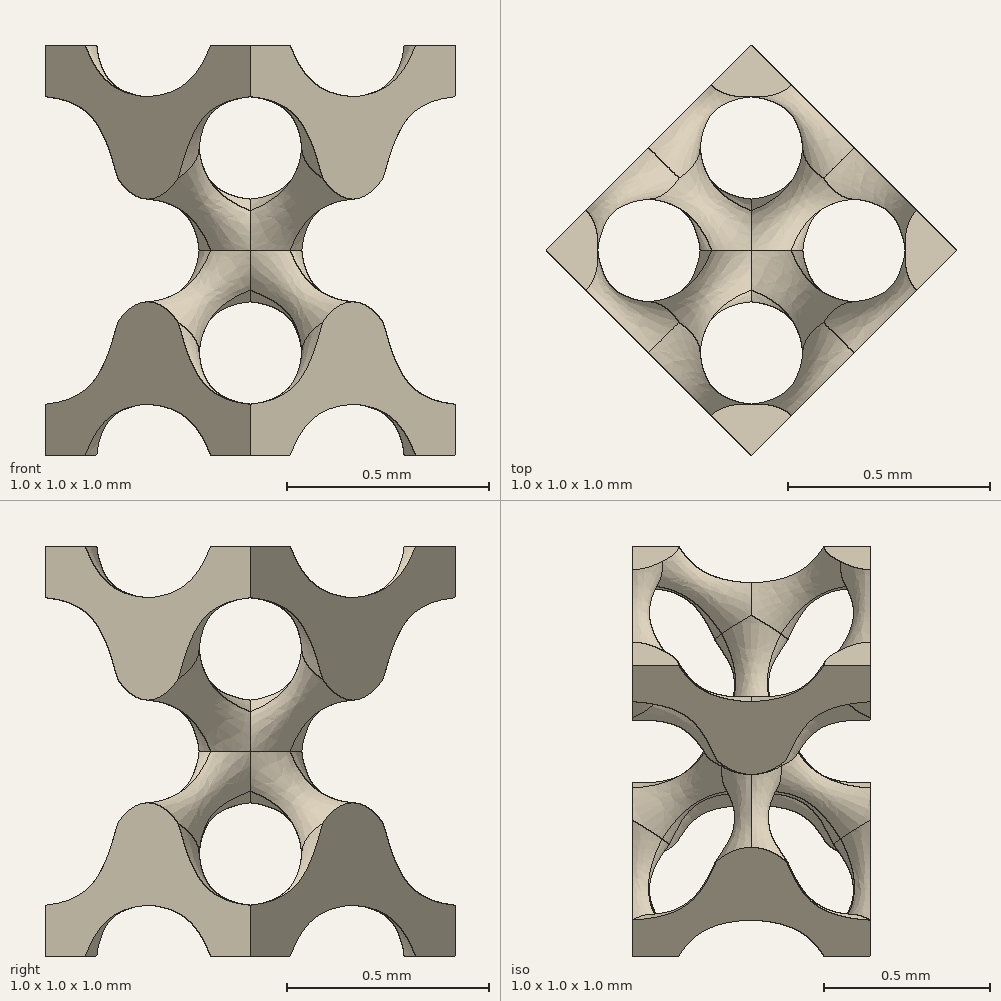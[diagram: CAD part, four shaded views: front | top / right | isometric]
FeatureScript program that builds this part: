
annotation { "Feature Type Name" : "Feature", "Feature Type Description" : "" }
export const myFeature = defineFeature(function(context is Context, id is Id, definition is map)
    precondition{}
    {
        {
            var Q0;
            Q0=qCreatedBy(makeId("Top.planeOp"),FACE);
            var sketch = newSketch(context, id + "F0", { "sketchPlane" : qUnion([Q0])});
            skPoint(sketch, "E0", {"position": v(0.5, 0) * mm});
            skPoint(sketch, "E1", {"position": v(0, -0.5) * mm});
            skLineSegment(sketch, "E2", {"start": v(0, 0) * mm, "end": v(0.5, 0) * mm, "construction": true});
            skLineSegment(sketch, "E3", {"start": v(0, 0) * mm, "end": v(0, -0.5) * mm, "construction": true});
            skSolve(sketch);
        }
        {
            var Q0;
            Q0=qCreatedBy(makeId("Front.planeOp"),FACE);
            cPlane(context, id + "F1", {"entities" : qUnion([Q0]), "cplaneType" : CPlaneType.OFFSET, "offset" : 0.25 * mm, "width" : 152.4 * mm, "height" : 152.4 * mm});
        }
        {
            var Q0;
            Q0=qCreatedBy(id+"F1.planeOp",FACE);
            var sketch = newSketch(context, id + "F2", { "sketchPlane" : qUnion([Q0])});
            skPoint(sketch, "E4", {"position": v(0.25, 0.25) * mm});
            skSolve(sketch);
        }
        {
            var Q0;
            Q0=qCreatedBy(makeId("Front.planeOp"),FACE);
            var sketch = newSketch(context, id + "F3", { "sketchPlane" : qUnion([Q0])});
            skPoint(sketch, "E5", {"position": v(0, 0.5) * mm});
            skSolve(sketch);
        }
        {
            var Q0;
            Q0=sQuery(id+"F3.wireOp",VERTEX,"E5");
            var Q1;
            Q1=qCreatedBy(makeId("Origin.pointOp"),VERTEX);
            var Q2;
            Q2=sQuery(id+"F2.wireOp",VERTEX,"E4");
            cPlane(context, id + "F4", {"entities" : qUnion([Q0, Q1, Q2]), "cplaneType" : CPlaneType.THREE_POINT, "offset" : 25.4 * mm, "width" : 152.4 * mm, "height" : 152.4 * mm});
        }
        {
            var Q0;
            Q0=qCreatedBy(id+"F4.planeOp",FACE);
            var sketch = newSketch(context, id + "F5", { "sketchPlane" : qUnion([Q0])});
            skLineSegment(sketch, "E6", {"start": v(0, 0.5) * mm, "end": v(-0.36, 0.25) * mm, "construction": true});
            skPoint(sketch, "E7", {"position": v(-0.18, 0.38) * mm});
            skLineSegment(sketch, "E8", {"start": v(0, 0.5) * mm, "end": v(-0.18, 0.38) * mm});
            skLineSegment(sketch, "E9", {"start": v(-0.18, 0.38) * mm, "end": v(-0.36, 0.25) * mm});
            skSolve(sketch);
        }
        {
            var Q0;
            Q0=sQuery(id+"F5.wireOp",VERTEX,"E6.start");
            var Q1;
            Q1=sQuery(id+"F5.wireOp",EDGE,"E6");
            cPlane(context, id + "F6", {"entities" : qUnion([Q0, Q1]), "cplaneType" : CPlaneType.LINE_POINT, "offset" : 25.4 * mm, "width" : 152.4 * mm, "height" : 152.4 * mm});
        }
        {
            var Q0;
            Q0=qCreatedBy(id+"F6.planeOp",FACE);
            var sketch = newSketch(context, id + "F7", { "sketchPlane" : qUnion([Q0])});
            skLineSegment(sketch, "E10", {"start": v(0.2, 0.36) * mm, "end": v(0.05, 0.36) * mm});
            skLineSegment(sketch, "E11", {"start": v(0.28, 0.23) * mm, "end": v(0.2, 0.36) * mm});
            skLineSegment(sketch, "E12", {"start": v(0.2, 0.36) * mm, "end": v(0.41, 0) * mm, "construction": true});
            skArc(sketch, "E13", {"start": v(0.28, 0.23) * mm, "mid": v(0.13, 0.23) * mm, "end": v(0.05, 0.36) * mm});
            skLineSegment(sketch, "E14", {"start": v(0.2, 0.36) * mm, "end": v(-0.2, 0.36) * mm, "construction": true});
            skSolve(sketch);
        }
        {
            var Q0;
            Q0=sQuery(id+"F5.wireOp",VERTEX,"E7");
            var Q1;
            Q1=sQuery(id+"F5.wireOp",EDGE,"E6");
            cPlane(context, id + "F8", {"entities" : qUnion([Q0, Q1]), "cplaneType" : CPlaneType.LINE_POINT, "offset" : 25.4 * mm, "width" : 152.4 * mm, "height" : 152.4 * mm});
        }
        {
            var Q0;
            Q0=qCreatedBy(id+"F8.planeOp",FACE);
            var sketch = newSketch(context, id + "F9", { "sketchPlane" : qUnion([Q0])});
            skLineSegment(sketch, "E15", {"start": v(0.16, 0.36) * mm, "end": v(0.2, 0.36) * mm});
            skLineSegment(sketch, "E16.MirrorCS", {"start": v(0.23, 0.32) * mm, "end": v(0.2, 0.36) * mm});
            skLineSegment(sketch, "E17", {"start": v(0.2, 0.36) * mm, "end": v(0.41, 0) * mm, "construction": true});
            skLineSegment(sketch, "E18", {"start": v(0.2, 0.36) * mm, "end": v(-0.2, 0.36) * mm, "construction": true});
            skArc(sketch, "E19", {"start": v(0.23, 0.32) * mm, "mid": v(0.18, 0.32) * mm, "end": v(0.16, 0.36) * mm});
            skSolve(sketch);
        }
        {
            var Q0;
            Q0=sQuery(id+"F2.wireOp",VERTEX,"E4");
            var Q1;
            Q1=sQuery(id+"F5.wireOp",EDGE,"E6");
            cPlane(context, id + "F10", {"entities" : qUnion([Q0, Q1]), "cplaneType" : CPlaneType.LINE_POINT, "offset" : 25.4 * mm, "width" : 152.4 * mm, "height" : 152.4 * mm});
        }
        {
            var Q0;
            Q0=qCreatedBy(id+"F10.planeOp",FACE);
            var sketch = newSketch(context, id + "F11", { "sketchPlane" : qUnion([Q0])});
            skLineSegment(sketch, "E20", {"start": v(0.05, 0.36) * mm, "end": v(0.2, 0.36) * mm});
            skLineSegment(sketch, "E21.MirrorCS", {"start": v(0.28, 0.23) * mm, "end": v(0.2, 0.36) * mm});
            skLineSegment(sketch, "E22", {"start": v(0.41, 0) * mm, "end": v(0.2, 0.36) * mm, "construction": true});
            skLineSegment(sketch, "E23", {"start": v(-0.2, 0.36) * mm, "end": v(0.2, 0.36) * mm, "construction": true});
            skArc(sketch, "E24", {"start": v(0.28, 0.23) * mm, "mid": v(0.13, 0.23) * mm, "end": v(0.05, 0.36) * mm});
            skSolve(sketch);
        }
        {
            var Q0;
            Q0=qSketchRegion(id+"F7",true);
            var Q1;
            Q1=qSketchRegion(id+"F9",true);
            var Q2;
            Q2=qSketchRegion(id+"F11",true);
            loft(context, id + "F12", {"sheetProfilesArray" : [{ "sheetProfileEntities" : qUnion([Q0]) }, { "sheetProfileEntities" : qUnion([Q1]) }, { "sheetProfileEntities" : qUnion([Q2]) }]});
        }
        {
            var Q0;
            Q0=sQuery(id+"F0.wireOp",VERTEX,"E1");
            var Q1;
            Q1=sQuery(id+"F0.wireOp",VERTEX,"E0");
            var Q2;
            Q2=sQuery(id+"F5.wireOp",VERTEX,"E8.start");
            cPlane(context, id + "F13", {"entities" : qUnion([Q0, Q1, Q2]), "cplaneType" : CPlaneType.THREE_POINT, "offset" : 25.4 * mm, "width" : 152.4 * mm, "height" : 152.4 * mm});
        }
        {
            var Q0;
            Q0=qCreatedBy(id+"F13.planeOp",FACE);
            var sketch = newSketch(context, id + "F14", { "sketchPlane" : qUnion([Q0])});
            skLineSegment(sketch, "E25", {"start": v(0, 0) * mm, "end": v(-0.41, 0) * mm, "construction": true});
            skLineSegment(sketch, "E26", {"start": v(0.2, -0.36) * mm, "end": v(-0.41, 0) * mm});
            skLineSegment(sketch, "E27", {"start": v(-0.41, 0) * mm, "end": v(-0.2, 0.36) * mm});
            skLineSegment(sketch, "E28", {"start": v(-0.2, 0.36) * mm, "end": v(0, 0) * mm});
            skLineSegment(sketch, "E29", {"start": v(0.2, -0.36) * mm, "end": v(0.41, 0) * mm});
            skLineSegment(sketch, "E30", {"start": v(0.41, 0) * mm, "end": v(0, 0) * mm});
            skSolve(sketch);
        }
        {
            var Q0;
            Q0=qSketchRegion(id+"F14",true);
            extrude(context, id + "F15", {"entities" : qUnion([Q0]), "operationType" : NewBodyOperationType.REMOVE, "endBound" : BoundingType.THROUGH_ALL, "oppositeDirection" : true, "depth" : 25.4 * mm, "hasSecondDirection" : true, "secondDirectionBound" : SecondDirectionBoundingType.THROUGH_ALL, "secondDirectionOppositeDirection" : false, "secondDirectionDepth" : 25.4 * mm});
        }
        {
            var Q0;
            Q0=qCreatedBy(makeId("Top.planeOp"),FACE);
            var sketch = newSketch(context, id + "F16", { "sketchPlane" : qUnion([Q0])});
            skLineSegment(sketch, "E31", {"start": v(0, 0) * mm, "end": v(0.17, 0) * mm});
            skLineSegment(sketch, "E32", {"start": v(0.17, 0) * mm, "end": v(0.17, 0.34) * mm});
            skLineSegment(sketch, "E33", {"start": v(0.17, 0.34) * mm, "end": v(-0.34, 0.34) * mm});
            skLineSegment(sketch, "E34", {"start": v(-0.34, 0.34) * mm, "end": v(-0.34, -0.17) * mm});
            skLineSegment(sketch, "E35", {"start": v(-0.34, -0.17) * mm, "end": v(0, -0.17) * mm});
            skLineSegment(sketch, "E36", {"start": v(0, -0.17) * mm, "end": v(0, 0) * mm});
            skSolve(sketch);
        }
        {
            var Q0;
            Q0=qSketchRegion(id+"F16",true);
            extrude(context, id + "F17", {"entities" : qUnion([Q0]), "operationType" : NewBodyOperationType.REMOVE, "endBound" : BoundingType.THROUGH_ALL, "depth" : 25.4 * mm});
        }
        {
            var Q0;
            Q0=makeQuery(id+"F12.opLoft","SWEPT_BODY",BODY,{"disambiguationData":[OSD([makeQuery(id+"F7.imprint","IMPRINT",FACE,{"disambiguationData":[TD([[makeQuery(id+"F7.imprint","IMPRINT",EDGE,{"derivedFrom":sQuery(id+"F7.wireOp",EDGE,"E10")}),1.0]])]}),sQuery(id+"F9.wireOp",EDGE,"GCmqOtqE-NeVT-EvFR-6nvD-PbH5UIOyADtR"),makeQuery(id+"F11.imprint","IMPRINT",FACE,{"disambiguationData":[TD([[makeQuery(id+"F11.imprint","IMPRINT",EDGE,{"derivedFrom":sQuery(id+"F11.wireOp",EDGE,"4osW1ktJ-JKXO-eWzK-s2aB-EjtUfTZE1sgZ")}),-1.0]])]})])]});
            var Q1;
            Q1=makeQuery(id+"F15.boolean.opBoolean","COPY",FACE,{"derivedFrom":makeQuery(id+"F15.opExtrude","SWEPT_FACE",FACE,{"disambiguationData":[OSD([sQuery(id+"F14.wireOp",EDGE,"E28")])]})});
            mirror(context, id + "F18", {"operationType" : NewBodyOperationType.ADD, "entities" : qUnion([Q0]), "mirrorPlane" : qUnion([Q1])});
        }
        {
            var Q0;
            Q0=makeQuery(id+"F12.opLoft","SWEPT_BODY",BODY,{"disambiguationData":[OSD([makeQuery(id+"F7.imprint","IMPRINT",FACE,{"disambiguationData":[TD([[makeQuery(id+"F7.imprint","IMPRINT",EDGE,{"derivedFrom":sQuery(id+"F7.wireOp",EDGE,"E10")}),1.0]])]}),sQuery(id+"F9.wireOp",EDGE,"GCmqOtqE-NeVT-EvFR-6nvD-PbH5UIOyADtR"),makeQuery(id+"F11.imprint","IMPRINT",FACE,{"disambiguationData":[TD([[makeQuery(id+"F11.imprint","IMPRINT",EDGE,{"derivedFrom":sQuery(id+"F11.wireOp",EDGE,"4osW1ktJ-JKXO-eWzK-s2aB-EjtUfTZE1sgZ")}),-1.0]])]})])]});
            var Q1;
            Q1=makeQuery(id+"F15.boolean.opBoolean","COPY",FACE,{"derivedFrom":makeQuery(id+"F15.opExtrude","SWEPT_FACE",FACE,{"disambiguationData":[OSD([sQuery(id+"F14.wireOp",EDGE,"E30")])]})});
            mirror(context, id + "F19", {"operationType" : NewBodyOperationType.ADD, "entities" : qUnion([Q0]), "mirrorPlane" : qUnion([Q1])});
        }
        {
            var Q0;
            Q0=makeQuery(id+"F12.opLoft","SWEPT_BODY",BODY,{"disambiguationData":[OSD([makeQuery(id+"F7.imprint","IMPRINT",FACE,{"disambiguationData":[TD([[makeQuery(id+"F7.imprint","IMPRINT",EDGE,{"derivedFrom":sQuery(id+"F7.wireOp",EDGE,"E10")}),1.0]])]}),sQuery(id+"F9.wireOp",EDGE,"GCmqOtqE-NeVT-EvFR-6nvD-PbH5UIOyADtR"),makeQuery(id+"F11.imprint","IMPRINT",FACE,{"disambiguationData":[TD([[makeQuery(id+"F11.imprint","IMPRINT",EDGE,{"derivedFrom":sQuery(id+"F11.wireOp",EDGE,"4osW1ktJ-JKXO-eWzK-s2aB-EjtUfTZE1sgZ")}),-1.0]])]})])]});
            var Q1;
            Q1=makeQuery(id+"F18.opPattern","COPY",FACE,{"derivedFrom":makeQuery(id+"F17.boolean.opBoolean","COPY",FACE,{"derivedFrom":makeQuery(id+"F17.opExtrude","SWEPT_FACE",FACE,{"disambiguationData":[OSD([sQuery(id+"F16.wireOp",EDGE,"E36")])]})}),"instanceName":"1"});
            mirror(context, id + "F20", {"operationType" : NewBodyOperationType.ADD, "entities" : qUnion([Q0]), "mirrorPlane" : qUnion([Q1])});
        }
        {
            var Q0;
            Q0=makeQuery(id+"F12.opLoft","SWEPT_BODY",BODY,{"disambiguationData":[OSD([makeQuery(id+"F7.imprint","IMPRINT",FACE,{"disambiguationData":[TD([[makeQuery(id+"F7.imprint","IMPRINT",EDGE,{"derivedFrom":sQuery(id+"F7.wireOp",EDGE,"E10")}),1.0]])]}),sQuery(id+"F9.wireOp",EDGE,"GCmqOtqE-NeVT-EvFR-6nvD-PbH5UIOyADtR"),makeQuery(id+"F11.imprint","IMPRINT",FACE,{"disambiguationData":[TD([[makeQuery(id+"F11.imprint","IMPRINT",EDGE,{"derivedFrom":sQuery(id+"F11.wireOp",EDGE,"4osW1ktJ-JKXO-eWzK-s2aB-EjtUfTZE1sgZ")}),-1.0]])]})])]});
            var Q1;
            {var subQ0=makeQuery(id+"F19.opPattern","COPY",FACE,{"derivedFrom":makeQuery(id+"F17.boolean.opBoolean","COPY",FACE,{"derivedFrom":makeQuery(id+"F17.opExtrude","SWEPT_FACE",FACE,{"disambiguationData":[OSD([sQuery(id+"F16.wireOp",EDGE,"E36")])]})}),"instanceName":"1"});Q1=makeQuery(id+"F20.boolean.opBoolean","MERGE",FACE,{"derivedFrom":[subQ0,makeQuery(id+"F20.opPattern","COPY",FACE,{"derivedFrom":subQ0,"instanceName":"1"})]});}
            mirror(context, id + "F21", {"operationType" : NewBodyOperationType.ADD, "entities" : qUnion([Q0]), "mirrorPlane" : qUnion([Q1])});
        }
        {
            var Q0;
            Q0=makeQuery(id+"F12.opLoft","SWEPT_BODY",BODY,{"disambiguationData":[OSD([makeQuery(id+"F7.imprint","IMPRINT",FACE,{"disambiguationData":[TD([[makeQuery(id+"F7.imprint","IMPRINT",EDGE,{"derivedFrom":sQuery(id+"F7.wireOp",EDGE,"E10")}),1.0]])]}),sQuery(id+"F9.wireOp",EDGE,"GCmqOtqE-NeVT-EvFR-6nvD-PbH5UIOyADtR"),makeQuery(id+"F11.imprint","IMPRINT",FACE,{"disambiguationData":[TD([[makeQuery(id+"F11.imprint","IMPRINT",EDGE,{"derivedFrom":sQuery(id+"F11.wireOp",EDGE,"4osW1ktJ-JKXO-eWzK-s2aB-EjtUfTZE1sgZ")}),-1.0]])]})])]});
            var Q1;
            {var subQ0=makeQuery(id+"F20.opPattern","COPY",FACE,{"derivedFrom":makeQuery(id+"F17.boolean.opBoolean","COPY",FACE,{"derivedFrom":makeQuery(id+"F17.opExtrude","SWEPT_FACE",FACE,{"disambiguationData":[OSD([sQuery(id+"F16.wireOp",EDGE,"E31")])]})}),"instanceName":"1"});Q1=makeQuery(id+"F21.boolean.opBoolean","MERGE",FACE,{"derivedFrom":[subQ0,makeQuery(id+"F21.opPattern","COPY",FACE,{"derivedFrom":subQ0,"instanceName":"1"})]});}
            mirror(context, id + "F22", {"operationType" : NewBodyOperationType.ADD, "entities" : qUnion([Q0]), "mirrorPlane" : qUnion([Q1])});
        }
        {
            var Q0;
            Q0=makeQuery(id+"F12.opLoft","SWEPT_BODY",BODY,{"disambiguationData":[OSD([makeQuery(id+"F7.imprint","IMPRINT",FACE,{"disambiguationData":[TD([[makeQuery(id+"F7.imprint","IMPRINT",EDGE,{"derivedFrom":sQuery(id+"F7.wireOp",EDGE,"E10")}),1.0]])]}),sQuery(id+"F9.wireOp",EDGE,"GCmqOtqE-NeVT-EvFR-6nvD-PbH5UIOyADtR"),makeQuery(id+"F11.imprint","IMPRINT",FACE,{"disambiguationData":[TD([[makeQuery(id+"F11.imprint","IMPRINT",EDGE,{"derivedFrom":sQuery(id+"F11.wireOp",EDGE,"4osW1ktJ-JKXO-eWzK-s2aB-EjtUfTZE1sgZ")}),-1.0]])]})])]});
            var Q1;
            {var subQ0=makeQuery(id+"F12.opLoft","SWEPT_FACE",FACE,{"disambiguationData":[OSD([sQuery(id+"F7.wireOp",EDGE,"E10"),sQuery(id+"F7.wireOp",EDGE,"vDo2YPjj-GWBM-UHMT-tmq4-Qm6dyUhXzKrZ"),sQuery(id+"F7.wireOp",EDGE,"E11"),sQuery(id+"F9.wireOp",EDGE,"E15"),sQuery(id+"F9.wireOp",EDGE,"E16.MirrorCS"),sQuery(id+"F9.wireOp",EDGE,"bbb26eb3-bb03-4cfc-8d6f-3f1ca2a9a7260.MirrorCS")])]});var subQ1=makeQuery(id+"F18.boolean.opBoolean","MERGE",FACE,{"derivedFrom":[subQ0,makeQuery(id+"F18.opPattern","COPY",FACE,{"derivedFrom":subQ0,"instanceName":"1"})]});Q1=makeQuery(id+"F22.boolean.opBoolean","MERGE",FACE,{"derivedFrom":[subQ1,makeQuery(id+"F22.opPattern","COPY",FACE,{"derivedFrom":subQ1,"instanceName":"1"})]});}
            mirror(context, id + "F23", {"operationType" : NewBodyOperationType.ADD, "entities" : qUnion([Q0]), "mirrorPlane" : qUnion([Q1])});
        }
        {
            var Q0;
            Q0=makeQuery(id+"F12.opLoft","SWEPT_BODY",BODY,{"disambiguationData":[OSD([makeQuery(id+"F7.imprint","IMPRINT",FACE,{"disambiguationData":[TD([[makeQuery(id+"F7.imprint","IMPRINT",EDGE,{"derivedFrom":sQuery(id+"F7.wireOp",EDGE,"E10")}),1.0]])]}),sQuery(id+"F9.wireOp",EDGE,"GCmqOtqE-NeVT-EvFR-6nvD-PbH5UIOyADtR"),makeQuery(id+"F11.imprint","IMPRINT",FACE,{"disambiguationData":[TD([[makeQuery(id+"F11.imprint","IMPRINT",EDGE,{"derivedFrom":sQuery(id+"F11.wireOp",EDGE,"4osW1ktJ-JKXO-eWzK-s2aB-EjtUfTZE1sgZ")}),-1.0]])]})])]});
            var Q1;
            {var subQ0=makeQuery(id+"F12.opLoft","SWEPT_FACE",FACE,{"disambiguationData":[OSD([sQuery(id+"F7.wireOp",EDGE,"E10"),sQuery(id+"F7.wireOp",EDGE,"b2Q6jkyI-x5VM-ItTv-5VdG-wCWcSs1pkRzT"),sQuery(id+"F7.wireOp",EDGE,"E11"),sQuery(id+"F9.wireOp",EDGE,"GCmqOtqE-NeVT-EvFR-6nvD-PbH5UIOyADtR"),sQuery(id+"F9.wireOp",EDGE,"E15"),sQuery(id+"F9.wireOp",EDGE,"E16.MirrorCS")])]});var subQ1=makeQuery(id+"F19.boolean.opBoolean","MERGE",FACE,{"derivedFrom":[subQ0,makeQuery(id+"F19.opPattern","COPY",FACE,{"derivedFrom":subQ0,"instanceName":"1"})]});Q1=makeQuery(id+"F21.boolean.opBoolean","MERGE",FACE,{"derivedFrom":[subQ1,makeQuery(id+"F21.opPattern","COPY",FACE,{"derivedFrom":subQ1,"instanceName":"1"})]});}
            mirror(context, id + "F24", {"operationType" : NewBodyOperationType.ADD, "entities" : qUnion([Q0]), "mirrorPlane" : qUnion([Q1])});
        }
        {
            var Q0;
            Q0=makeQuery(id+"F12.opLoft","SWEPT_BODY",BODY,{"disambiguationData":[OSD([makeQuery(id+"F7.imprint","IMPRINT",FACE,{"disambiguationData":[TD([[makeQuery(id+"F7.imprint","IMPRINT",EDGE,{"derivedFrom":sQuery(id+"F7.wireOp",EDGE,"E10")}),1.0]])]}),sQuery(id+"F9.wireOp",EDGE,"GCmqOtqE-NeVT-EvFR-6nvD-PbH5UIOyADtR"),makeQuery(id+"F11.imprint","IMPRINT",FACE,{"disambiguationData":[TD([[makeQuery(id+"F11.imprint","IMPRINT",EDGE,{"derivedFrom":sQuery(id+"F11.wireOp",EDGE,"4osW1ktJ-JKXO-eWzK-s2aB-EjtUfTZE1sgZ")}),-1.0]])]})])]});
            var Q1;
            {var subQ0=makeQuery(id+"F12.opLoft","SWEPT_FACE",FACE,{"disambiguationData":[OSD([sQuery(id+"F7.wireOp",EDGE,"E10"),sQuery(id+"F7.wireOp",EDGE,"vDo2YPjj-GWBM-UHMT-tmq4-Qm6dyUhXzKrZ"),sQuery(id+"F7.wireOp",EDGE,"E11"),sQuery(id+"F9.wireOp",EDGE,"E15"),sQuery(id+"F9.wireOp",EDGE,"E16.MirrorCS"),sQuery(id+"F9.wireOp",EDGE,"bbb26eb3-bb03-4cfc-8d6f-3f1ca2a9a7260.MirrorCS")])]});var subQ1=makeQuery(id+"F21.opPattern","COPY",FACE,{"derivedFrom":makeQuery(id+"F18.boolean.opBoolean","MERGE",FACE,{"derivedFrom":[subQ0,makeQuery(id+"F18.opPattern","COPY",FACE,{"derivedFrom":subQ0,"instanceName":"1"})]}),"instanceName":"1"});Q1=makeQuery(id+"F22.boolean.opBoolean","MERGE",FACE,{"derivedFrom":[subQ1,makeQuery(id+"F22.opPattern","COPY",FACE,{"derivedFrom":subQ1,"instanceName":"1"})]});}
            mirror(context, id + "F25", {"operationType" : NewBodyOperationType.ADD, "entities" : qUnion([Q0]), "mirrorPlane" : qUnion([Q1])});
        }
        {
            var Q0;
            Q0=makeQuery(id+"F12.opLoft","SWEPT_BODY",BODY,{"disambiguationData":[OSD([makeQuery(id+"F7.imprint","IMPRINT",FACE,{"disambiguationData":[TD([[makeQuery(id+"F7.imprint","IMPRINT",EDGE,{"derivedFrom":sQuery(id+"F7.wireOp",EDGE,"E10")}),1.0]])]}),sQuery(id+"F9.wireOp",EDGE,"GCmqOtqE-NeVT-EvFR-6nvD-PbH5UIOyADtR"),makeQuery(id+"F11.imprint","IMPRINT",FACE,{"disambiguationData":[TD([[makeQuery(id+"F11.imprint","IMPRINT",EDGE,{"derivedFrom":sQuery(id+"F11.wireOp",EDGE,"4osW1ktJ-JKXO-eWzK-s2aB-EjtUfTZE1sgZ")}),-1.0]])]})])]});
            var Q1;
            {var subQ0=makeQuery(id+"F12.opLoft","SWEPT_FACE",FACE,{"disambiguationData":[OSD([sQuery(id+"F7.wireOp",EDGE,"E10"),sQuery(id+"F7.wireOp",EDGE,"b2Q6jkyI-x5VM-ItTv-5VdG-wCWcSs1pkRzT"),sQuery(id+"F7.wireOp",EDGE,"E11"),sQuery(id+"F9.wireOp",EDGE,"GCmqOtqE-NeVT-EvFR-6nvD-PbH5UIOyADtR"),sQuery(id+"F9.wireOp",EDGE,"E15"),sQuery(id+"F9.wireOp",EDGE,"E16.MirrorCS")])]});var subQ1=makeQuery(id+"F19.boolean.opBoolean","MERGE",FACE,{"derivedFrom":[subQ0,makeQuery(id+"F19.opPattern","COPY",FACE,{"derivedFrom":subQ0,"instanceName":"1"})]});Q1=makeQuery(id+"F22.opPattern","COPY",FACE,{"derivedFrom":makeQuery(id+"F21.boolean.opBoolean","MERGE",FACE,{"derivedFrom":[subQ1,makeQuery(id+"F21.opPattern","COPY",FACE,{"derivedFrom":subQ1,"instanceName":"1"})]}),"instanceName":"1"});}
            mirror(context, id + "F26", {"operationType" : NewBodyOperationType.ADD, "entities" : qUnion([Q0]), "mirrorPlane" : qUnion([Q1])});
        }
        {
            var Q0;
            Q0=qCreatedBy(makeId("Right.planeOp"),FACE);
            var sketch = newSketch(context, id + "F27", { "sketchPlane" : qUnion([Q0])});
            skLineSegment(sketch, "E37.bottom", {"start": v(0.5, 0) * mm, "end": v(-0.5, 0) * mm});
            skLineSegment(sketch, "E37.top", {"start": v(0.5, 1.02) * mm, "end": v(-0.5, 1.02) * mm});
            skLineSegment(sketch, "E37.left", {"start": v(0.5, 0) * mm, "end": v(0.5, 1.02) * mm});
            skLineSegment(sketch, "E37.right", {"start": v(-0.5, 0) * mm, "end": v(-0.5, 1.02) * mm});
            skSolve(sketch);
        }
        {
            var Q0;
            Q0=qSketchRegion(id+"F27",true);
            extrude(context, id + "F28", {"entities" : qUnion([Q0]), "operationType" : NewBodyOperationType.INTERSECT, "endBound" : BoundingType.THROUGH_ALL, "depth" : 25.4 * mm, "hasSecondDirection" : true, "secondDirectionBound" : SecondDirectionBoundingType.THROUGH_ALL, "secondDirectionOppositeDirection" : true, "secondDirectionDepth" : 25.4 * mm});
        }
        {
            var Q0;
            Q0=qCreatedBy(makeId("Top.planeOp"),FACE);
            var sketch = newSketch(context, id + "F29", { "sketchPlane" : qUnion([Q0])});
            skLineSegment(sketch, "E38", {"start": v(-0.5, 0) * mm, "end": v(0, 0.5) * mm});
            skLineSegment(sketch, "E39", {"start": v(0, 0.5) * mm, "end": v(0.5, 0) * mm});
            skLineSegment(sketch, "E40", {"start": v(0.5, 0) * mm, "end": v(0, -0.5) * mm});
            skLineSegment(sketch, "E41", {"start": v(0, -0.5) * mm, "end": v(-0.5, 0) * mm});
            skSolve(sketch);
        }
        {
            var Q0;
            Q0=qSketchRegion(id+"F29",true);
            extrude(context, id + "F30", {"entities" : qUnion([Q0]), "operationType" : NewBodyOperationType.INTERSECT, "endBound" : BoundingType.THROUGH_ALL, "depth" : 25.4 * mm, "hasSecondDirection" : true, "secondDirectionBound" : SecondDirectionBoundingType.THROUGH_ALL, "secondDirectionOppositeDirection" : true, "secondDirectionDepth" : 25.4 * mm});
        }
    });
